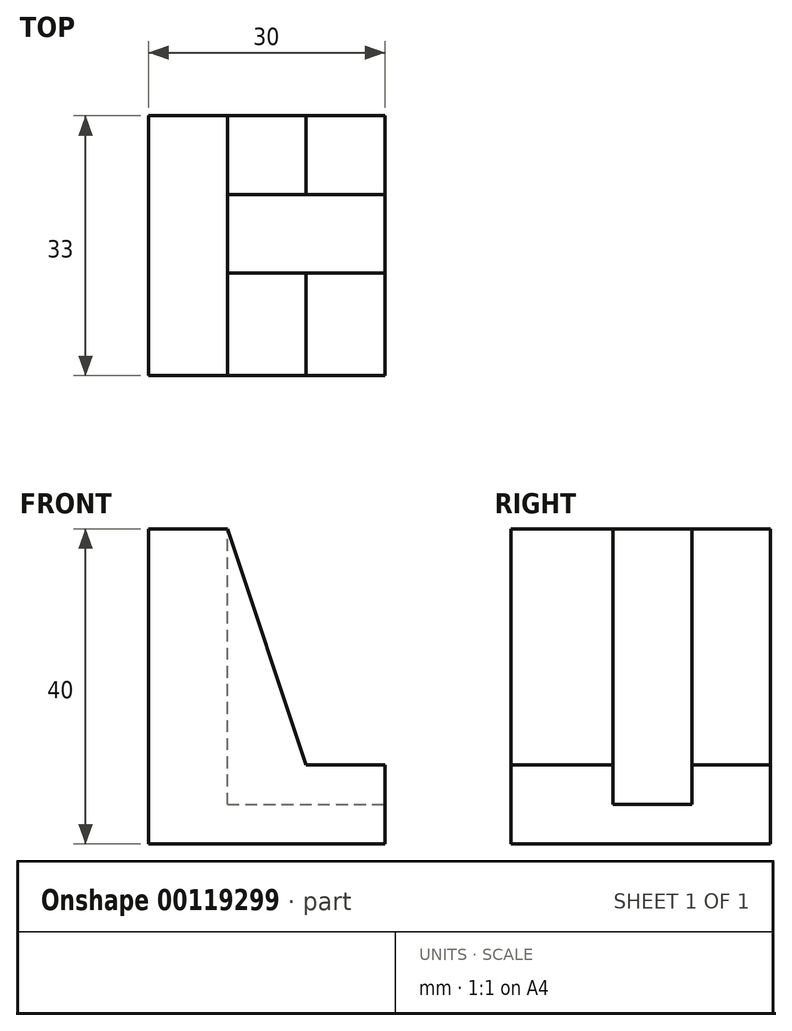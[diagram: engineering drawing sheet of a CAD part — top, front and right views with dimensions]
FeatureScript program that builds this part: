
annotation { "Feature Type Name" : "Feature", "Feature Type Description" : "" }
export const myFeature = defineFeature(function(context is Context, id is Id, definition is map)
    precondition{}
    {
        {
            var Q0;
            Q0=qCreatedBy(makeId("Front.planeOp"),FACE);
            var sketch = newSketch(context, id + "F0", { "sketchPlane" : qUnion([Q0])});
            skLineSegment(sketch, "E0", {"start": v(0, 0) * mm, "end": v(0, 40) * mm});
            skLineSegment(sketch, "E1", {"start": v(0, 40) * mm, "end": v(10, 40) * mm});
            skLineSegment(sketch, "E2", {"start": v(0, 0) * mm, "end": v(30, 0) * mm});
            skLineSegment(sketch, "E3", {"start": v(30, 0) * mm, "end": v(30, 10) * mm});
            skLineSegment(sketch, "E4", {"start": v(30, 10) * mm, "end": v(20, 10) * mm});
            skLineSegment(sketch, "E5", {"start": v(10, 40) * mm, "end": v(20, 10) * mm});
            skSolve(sketch);
        }
        {
            var Q0;
            Q0=makeQuery(id+"F0.imprint","IMPRINT",FACE,{"disambiguationData":[TD([[makeQuery(id+"F0.imprint","IMPRINT",EDGE,{"derivedFrom":sQuery(id+"F0.wireOp",EDGE,"E0")}),-1.0]])]});
            extrude(context, id + "F1", {"entities" : qUnion([Q0]), "depth" : 3 * mm});
        }
        {
            var Q0;
            Q0=makeQuery(id+"F1.opExtrude","CAP_FACE",FACE,{"disambiguationData":[OSD([sQuery(id+"F0.wireOp",EDGE,"E0"),sQuery(id+"F0.wireOp",EDGE,"E1"),sQuery(id+"F0.wireOp",EDGE,"E2"),sQuery(id+"F0.wireOp",EDGE,"E3"),sQuery(id+"F0.wireOp",EDGE,"E4"),sQuery(id+"F0.wireOp",EDGE,"E5")])],"isStart":false});
            extrude(context, id + "F2", {"entities" : qUnion([Q0]), "operationType" : NewBodyOperationType.ADD, "depth" : 30 * mm});
        }
        {
            var Q0;
            {var subQ0=sQuery(id+"F0.wireOp",EDGE,"E1");Q0=makeQuery(id+"F2.boolean.opBoolean","MERGE",FACE,{"derivedFrom":[makeQuery(id+"F1.opExtrude","SWEPT_FACE",FACE,{"disambiguationData":[OSD([subQ0])]}),makeQuery(id+"F2.opExtrude","SWEPT_FACE",FACE,{"disambiguationData":[OSD([subQ0])]})]});}
            var sketch = newSketch(context, id + "F3", { "sketchPlane" : qUnion([Q0])});
            skLineSegment(sketch, "E6.bottom", {"start": v(10, -10) * mm, "end": v(30, -10) * mm});
            skLineSegment(sketch, "E6.top", {"start": v(10, -20) * mm, "end": v(30, -20) * mm});
            skLineSegment(sketch, "E6.left", {"start": v(10, -10) * mm, "end": v(10, -20) * mm});
            skLineSegment(sketch, "E6.right", {"start": v(30, -10) * mm, "end": v(30, -20) * mm});
            skSolve(sketch);
        }
        {
            var Q0;
            Q0=makeQuery(id+"F3.imprint","IMPRINT",FACE,{"disambiguationData":[TD([[makeQuery(id+"F3.imprint","IMPRINT",EDGE,{"derivedFrom":sQuery(id+"F3.wireOp",EDGE,"E6.bottom")}),-1.0]])]});
            extrude(context, id + "F4", {"entities" : qUnion([Q0]), "operationType" : NewBodyOperationType.REMOVE, "oppositeDirection" : true, "depth" : 35 * mm});
        }
    });
